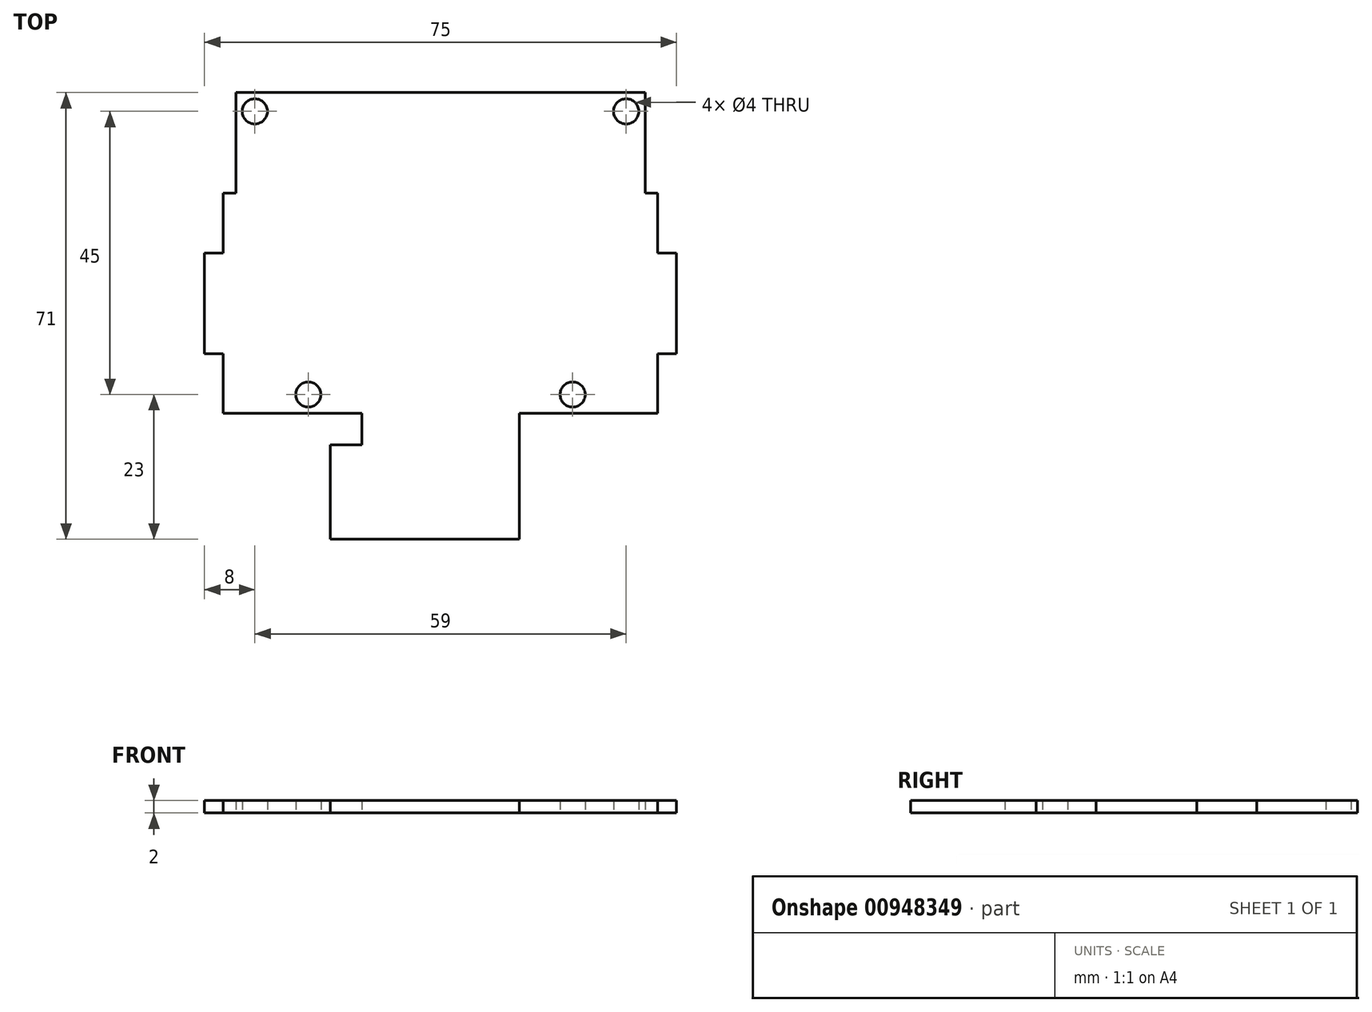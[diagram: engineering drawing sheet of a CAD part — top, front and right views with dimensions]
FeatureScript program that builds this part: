
annotation { "Feature Type Name" : "Feature", "Feature Type Description" : "" }
export const myFeature = defineFeature(function(context is Context, id is Id, definition is map)
    precondition{}
    {
        {
            var Q0;
            Q0=qCreatedBy(makeId("Top.planeOp"),FACE);
            var sketch = newSketch(context, id + "F0", { "sketchPlane" : qUnion([Q0])});
            skLineSegment(sketch, "E0.bottom", {"start": v(32.5, 25.5) * mm, "end": v(-32.5, 25.5) * mm});
            skLineSegment(sketch, "E0.top", {"start": v(32.5, -25.5) * mm, "end": v(-32.5, -25.5) * mm});
            skLineSegment(sketch, "E0.left", {"start": v(32.5, 25.5) * mm, "end": v(32.5, -25.5) * mm});
            skLineSegment(sketch, "E0.right", {"start": v(-32.5, 25.5) * mm, "end": v(-32.5, -25.5) * mm});
            skPoint(sketch, "E0.middle", {"position": v(0, 0) * mm});
            skCircle(sketch, "E1", {"center": v(29.5, 22.5) * mm, "radius": 2 * mm});
            skCircle(sketch, "E2", {"center": v(21, -22.5) * mm, "radius": 2 * mm});
            skCircle(sketch, "E3", {"center": v(-21, -22.5) * mm, "radius": 2 * mm});
            skCircle(sketch, "E4", {"center": v(-29.5, 22.5) * mm, "radius": 2 * mm});
            skLineSegment(sketch, "E5", {"start": v(32.5, -25.5) * mm, "end": v(34.5, -25.5) * mm});
            skLineSegment(sketch, "E6", {"start": v(34.5, -25.5) * mm, "end": v(34.5, -16) * mm});
            skLineSegment(sketch, "E7", {"start": v(34.5, -16) * mm, "end": v(37.5, -16) * mm});
            skLineSegment(sketch, "E8", {"start": v(37.5, -16) * mm, "end": v(37.5, 0) * mm});
            skLineSegment(sketch, "E9", {"start": v(37.5, 0) * mm, "end": v(34.5, 0) * mm});
            skLineSegment(sketch, "E10", {"start": v(34.5, 0) * mm, "end": v(34.5, 9.5) * mm});
            skLineSegment(sketch, "E11", {"start": v(34.5, 9.5) * mm, "end": v(32.5, 9.5) * mm});
            skLineSegment(sketch, "E12", {"start": v(-32.5, -25.5) * mm, "end": v(-34.5, -25.5) * mm});
            skLineSegment(sketch, "E13", {"start": v(-34.5, -25.5) * mm, "end": v(-34.5, -16) * mm});
            skLineSegment(sketch, "E14", {"start": v(-34.5, -16) * mm, "end": v(-37.5, -16) * mm});
            skLineSegment(sketch, "E15", {"start": v(-37.5, -16) * mm, "end": v(-37.5, 0) * mm});
            skLineSegment(sketch, "E16", {"start": v(-37.5, 0) * mm, "end": v(-34.5, 0) * mm});
            skLineSegment(sketch, "E17", {"start": v(-34.5, 0) * mm, "end": v(-34.5, 9.5) * mm});
            skLineSegment(sketch, "E18", {"start": v(-34.5, 9.5) * mm, "end": v(-32.5, 9.5) * mm});
            skLineSegment(sketch, "E19", {"start": v(12.5, -25.5) * mm, "end": v(12.5, -45.5) * mm});
            skLineSegment(sketch, "E20", {"start": v(12.5, -45.5) * mm, "end": v(-17.5, -45.5) * mm});
            skLineSegment(sketch, "E21", {"start": v(-17.5, -45.5) * mm, "end": v(-17.5, -30.5) * mm});
            skLineSegment(sketch, "E22", {"start": v(-17.5, -30.5) * mm, "end": v(-12.5, -30.5) * mm});
            skLineSegment(sketch, "E23", {"start": v(-12.5, -30.5) * mm, "end": v(-12.5, -25.5) * mm});
            skPoint(sketch, "E24.orphan", {"position": v(-17.5, -25.5) * mm});
            skSolve(sketch);
        }
        {
            var Q0;
            Q0 = qSketchRegion(id + "F0", true);
            extrude(context, id + "F1", {"entities" : qUnion([Q0]), "depth" : 2 * mm, "offsetDistance" : 25 * mm});
        }
    });
